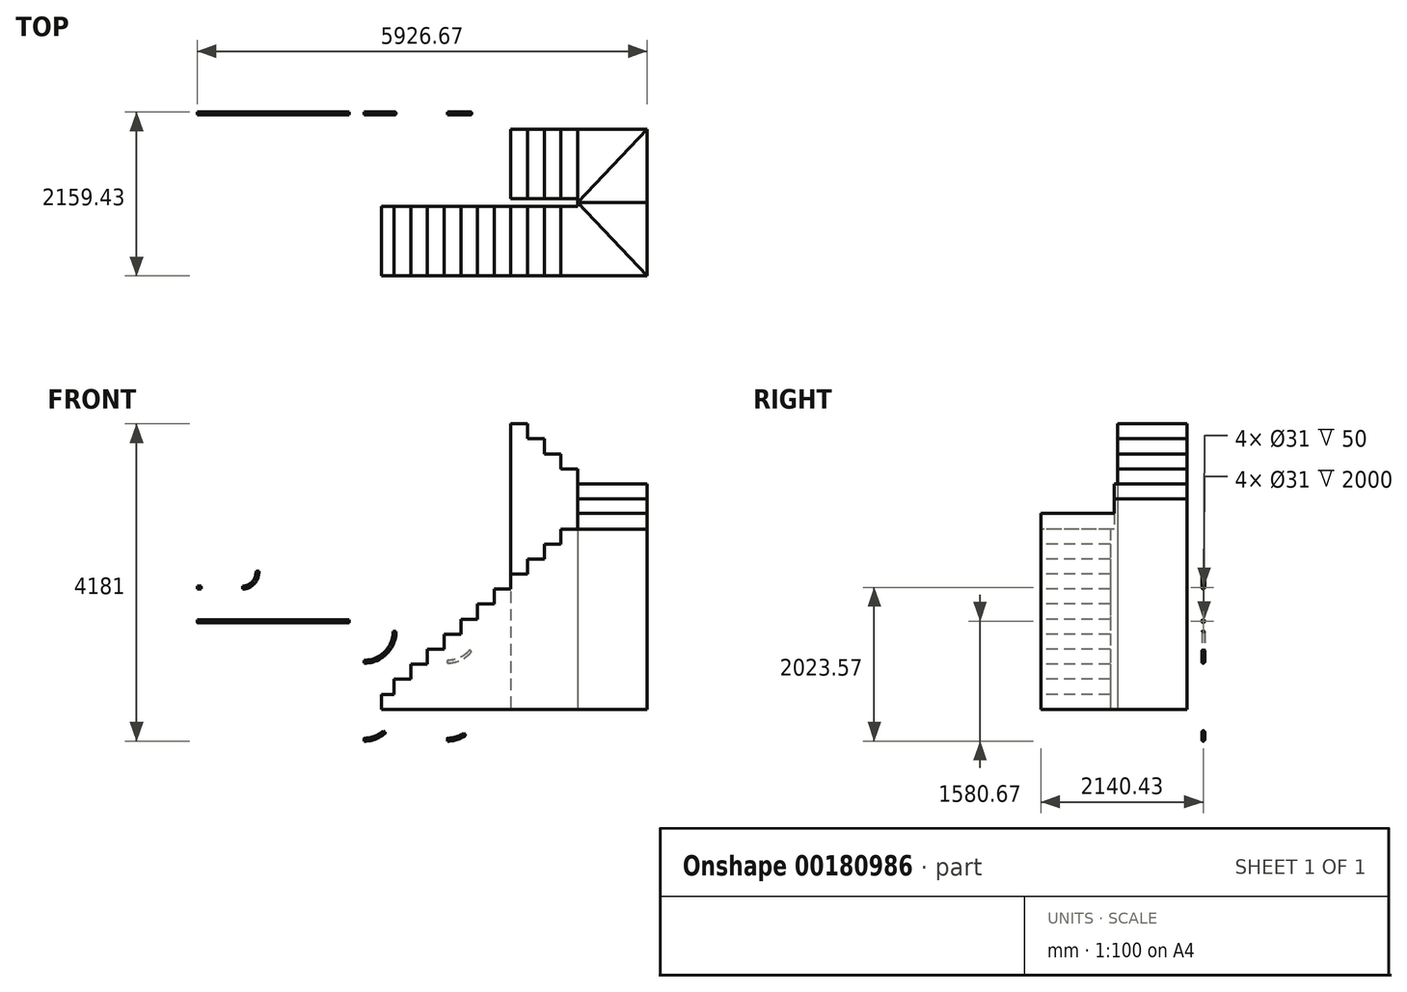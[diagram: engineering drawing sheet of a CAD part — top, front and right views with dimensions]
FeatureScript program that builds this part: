
annotation { "Feature Type Name" : "Feature", "Feature Type Description" : "" }
export const myFeature = defineFeature(function(context is Context, id is Id, definition is map)
    precondition{}
    {
        {
            var Q0;
            Q0=qCreatedBy(makeId("Front.planeOp"),FACE);
            var sketch = newSketch(context, id + "F0", { "sketchPlane" : qUnion([Q0])});
            skArc(sketch, "E0", {"start": v(-72.1, -400) * mm, "mid": v(71.25, -373.43) * mm, "end": v(195.56, -297.26) * mm});
            skArc(sketch, "E1", {"start": v(1022.64, -400) * mm, "mid": v(1142.93, -381.49) * mm, "end": v(1252.07, -327.66) * mm});
            skArc(sketch, "E2", {"start": v(-72.1, 626.56) * mm, "mid": v(210.75, 743.72) * mm, "end": v(327.9, 1026.56) * mm});
            skArc(sketch, "E3", {"start": v(1022.64, 626.56) * mm, "mid": v(1191.7, 664.04) * mm, "end": v(1329.06, 769.45) * mm});
            skLineSegment(sketch, "E4", {"start": v(-72.1, 645.56) * mm, "end": v(-72.1, 607.56) * mm});
            skLineSegment(sketch, "E5", {"start": v(308.9, 1026.56) * mm, "end": v(346.9, 1026.56) * mm});
            skLineSegment(sketch, "E6", {"start": v(-72.1, -381) * mm, "end": v(-72.1, -419) * mm});
            skLineSegment(sketch, "E7", {"start": v(182.84, -283.14) * mm, "end": v(208.27, -311.38) * mm});
            skLineSegment(sketch, "E8", {"start": v(1022.64, 645.56) * mm, "end": v(1022.64, 607.56) * mm});
            skLineSegment(sketch, "E9", {"start": v(1314.5, 781.66) * mm, "end": v(1343.62, 757.24) * mm});
            skLineSegment(sketch, "E10", {"start": v(1022.64, -381) * mm, "end": v(1022.64, -419) * mm});
            skLineSegment(sketch, "E11", {"start": v(1241.18, -312.1) * mm, "end": v(1262.97, -343.22) * mm});
            skArc(sketch, "E12.0", {"start": v(-72.1, 607.56) * mm, "mid": v(224.18, 730.29) * mm, "end": v(346.9, 1026.56) * mm});
            skArc(sketch, "E13.0", {"start": v(-72.1, 645.56) * mm, "mid": v(197.31, 757.16) * mm, "end": v(308.9, 1026.56) * mm});
            skArc(sketch, "E14.0", {"start": v(1022.64, 607.56) * mm, "mid": v(1199.72, 646.82) * mm, "end": v(1343.62, 757.24) * mm});
            skArc(sketch, "E15.0", {"start": v(1022.64, 645.56) * mm, "mid": v(1183.66, 681.26) * mm, "end": v(1314.5, 781.66) * mm});
            skArc(sketch, "E16.0", {"start": v(1022.64, -419) * mm, "mid": v(1148.64, -399.6) * mm, "end": v(1262.97, -343.22) * mm});
            skArc(sketch, "E17.0", {"start": v(1022.64, -381) * mm, "mid": v(1137.21, -363.37) * mm, "end": v(1241.18, -312.1) * mm});
            skArc(sketch, "E18.0", {"start": v(-72.1, -419) * mm, "mid": v(78.06, -391.17) * mm, "end": v(208.27, -311.38) * mm});
            skArc(sketch, "E19.0", {"start": v(-72.1, -381) * mm, "mid": v(64.44, -355.7) * mm, "end": v(182.84, -283.14) * mm});
            skSolve(sketch);
        }
        {
            var Q0;
            Q0=sQuery(id+"F0.wireOp",VERTEX,"E2.start");
            var Q1;
            Q1=qCreatedBy(makeId("Right.planeOp"),FACE);
            cPlane(context, id + "F1", {"entities" : qUnion([Q0, Q1]), "cplaneType" : CPlaneType.PLANE_POINT, "offset" : 25 * mm, "width" : 150 * mm, "height" : 150 * mm});
        }
        {
            var Q0;
            Q0=qCreatedBy(id+"F1.planeOp",FACE);
            var sketch = newSketch(context, id + "F2", { "sketchPlane" : qUnion([Q0])});
            skCircle(sketch, "E20", {"center": v(0, 626.56) * mm, "radius": 19 * mm});
            skCircle(sketch, "E21.0", {"center": v(0, 626.56) * mm, "radius": 15.5 * mm});
            skSolve(sketch);
        }
        {
            var Q0;
            Q0=qCreatedBy(makeId("Right.planeOp"),FACE);
            var Q1;
            Q1=sQuery(id+"F0.wireOp",VERTEX,"E0.start");
            cPlane(context, id + "F3", {"entities" : qUnion([Q0, Q1]), "cplaneType" : CPlaneType.PLANE_POINT, "offset" : 25 * mm, "width" : 150 * mm, "height" : 150 * mm});
        }
        {
            var Q0;
            Q0=qCreatedBy(id+"F3.planeOp",FACE);
            var sketch = newSketch(context, id + "F4", { "sketchPlane" : qUnion([Q0])});
            skCircle(sketch, "E22", {"center": v(0, -400) * mm, "radius": 19 * mm});
            skCircle(sketch, "E23.0", {"center": v(0, -400) * mm, "radius": 15.2 * mm});
            skSolve(sketch);
        }
        {
            var Q0;
            Q0=qCreatedBy(makeId("Right.planeOp"),FACE);
            var Q1;
            Q1=sQuery(id+"F0.wireOp",VERTEX,"E3.start");
            cPlane(context, id + "F5", {"entities" : qUnion([Q0, Q1]), "cplaneType" : CPlaneType.PLANE_POINT, "offset" : 25 * mm, "width" : 150 * mm, "height" : 150 * mm});
        }
        {
            var Q0;
            Q0=qCreatedBy(id+"F5.planeOp",FACE);
            var sketch = newSketch(context, id + "F6", { "sketchPlane" : qUnion([Q0])});
            skCircle(sketch, "E24", {"center": v(0, 626.56) * mm, "radius": 19 * mm});
            skCircle(sketch, "E25.0", {"center": v(0, 626.56) * mm, "radius": 15.5 * mm});
            skSolve(sketch);
        }
        {
            var Q0;
            Q0=sQuery(id+"F0.wireOp",VERTEX,"E1.start");
            var Q1;
            Q1=qCreatedBy(makeId("Right.planeOp"),FACE);
            cPlane(context, id + "F7", {"entities" : qUnion([Q0, Q1]), "cplaneType" : CPlaneType.PLANE_POINT, "offset" : 25 * mm, "width" : 150 * mm, "height" : 150 * mm});
        }
        {
            var Q0;
            Q0=qCreatedBy(id+"F7.planeOp",FACE);
            var sketch = newSketch(context, id + "F8", { "sketchPlane" : qUnion([Q0])});
            skCircle(sketch, "E26", {"center": v(0, -400) * mm, "radius": 19 * mm});
            skCircle(sketch, "E27.0", {"center": v(0, -400) * mm, "radius": 15.5 * mm});
            skSolve(sketch);
        }
        {
            var Q0;
            Q0=makeQuery(id+"F8.imprint","IMPRINT",FACE,{"disambiguationData":[TD([[makeQuery(id+"F8.imprint","IMPRINT",EDGE,{"derivedFrom":sQuery(id+"F8.wireOp",EDGE,"E26")}),1.0]])]});
            var Q1;
            Q1=sQuery(id+"F0.wireOp",EDGE,"E1");
            sweep(context, id + "F9", {"profiles" : qUnion([Q0]), "path" : qUnion([Q1])});
        }
        {
            var Q0;
            Q0=makeQuery(id+"F6.imprint","IMPRINT",FACE,{"disambiguationData":[TD([[makeQuery(id+"F6.imprint","IMPRINT",EDGE,{"derivedFrom":sQuery(id+"F6.wireOp",EDGE,"E24")}),1.0]])]});
            var Q1;
            Q1=sQuery(id+"F0.wireOp",EDGE,"E3");
            sweep(context, id + "F10", {"profiles" : qUnion([Q0]), "path" : qUnion([Q1])});
        }
        {
            var Q0;
            Q0=makeQuery(id+"F2.imprint","IMPRINT",FACE,{"disambiguationData":[TD([[makeQuery(id+"F2.imprint","IMPRINT",EDGE,{"derivedFrom":sQuery(id+"F2.wireOp",EDGE,"E20")}),1.0]])]});
            var Q1;
            Q1=sQuery(id+"F0.wireOp",EDGE,"E2");
            sweep(context, id + "F11", {"profiles" : qUnion([Q0]), "path" : qUnion([Q1])});
        }
        {
            var Q0;
            Q0=makeQuery(id+"F4.imprint","IMPRINT",FACE,{"disambiguationData":[TD([[makeQuery(id+"F4.imprint","IMPRINT",EDGE,{"derivedFrom":sQuery(id+"F4.wireOp",EDGE,"E22")}),1.0]])]});
            var Q1;
            Q1=sQuery(id+"F0.wireOp",EDGE,"E0");
            sweep(context, id + "F12", {"profiles" : qUnion([Q0]), "path" : qUnion([Q1])});
        }
        {
            var Q0;
            Q0=qCreatedBy(makeId("Top.planeOp"),FACE);
            var sketch = newSketch(context, id + "F13", { "sketchPlane" : qUnion([Q0])});
            skLineSegment(sketch, "E28.bottom", {"start": v(155.18, -210.43) * mm, "end": v(3655.18, -210.43) * mm});
            skLineSegment(sketch, "E28.top", {"start": v(155.18, -2140.43) * mm, "end": v(3655.18, -2140.43) * mm});
            skLineSegment(sketch, "E28.left", {"start": v(155.18, -210.43) * mm, "end": v(155.18, -2140.43) * mm});
            skLineSegment(sketch, "E28.right", {"start": v(3655.18, -210.43) * mm, "end": v(3655.18, -2140.43) * mm});
            skLineSegment(sketch, "E29", {"start": v(155.18, -1175.43) * mm, "end": v(2740.18, -1175.43) * mm, "construction": true});
            skLineSegment(sketch, "E30", {"start": v(155.18, -1125.43) * mm, "end": v(2740.18, -1125.43) * mm});
            skLineSegment(sketch, "E31", {"start": v(2740.18, -1125.43) * mm, "end": v(2740.18, -1175.43) * mm});
            skLineSegment(sketch, "E32", {"start": v(155.18, -1225.43) * mm, "end": v(2740.18, -1225.43) * mm});
            skLineSegment(sketch, "E33", {"start": v(2740.18, -1225.43) * mm, "end": v(2740.18, -1175.43) * mm});
            skLineSegment(sketch, "E34", {"start": v(2740.18, -1125.43) * mm, "end": v(2740.18, -210.43) * mm});
            skLineSegment(sketch, "E35", {"start": v(2740.18, -1225.43) * mm, "end": v(2740.18, -2140.43) * mm});
            skLineSegment(sketch, "E36", {"start": v(2740.18, -1175.43) * mm, "end": v(3655.18, -210.43) * mm});
            skLineSegment(sketch, "E37", {"start": v(2740.18, -1175.43) * mm, "end": v(3655.18, -2140.43) * mm});
            skPoint(sketch, "E38.orphan", {"position": v(3655.18, -1175.43) * mm});
            skLineSegment(sketch, "E39", {"start": v(2740.18, -1175.43) * mm, "end": v(3655.18, -1175.43) * mm});
            skLineSegment(sketch, "E40", {"start": v(2520.18, -210.43) * mm, "end": v(2520.18, -2140.43) * mm});
            skLineSegment(sketch, "E41", {"start": v(2300.18, -210.43) * mm, "end": v(2300.18, -2140.43) * mm});
            skLineSegment(sketch, "E42", {"start": v(2080.18, -210.43) * mm, "end": v(2080.18, -2140.43) * mm});
            skLineSegment(sketch, "E43", {"start": v(1860.18, -210.43) * mm, "end": v(1860.18, -2140.43) * mm});
            skLineSegment(sketch, "E44", {"start": v(1640.18, -210.43) * mm, "end": v(1640.18, -2140.43) * mm});
            skLineSegment(sketch, "E45", {"start": v(1420.18, -210.43) * mm, "end": v(1420.18, -2140.43) * mm});
            skLineSegment(sketch, "E46", {"start": v(1200.18, -210.43) * mm, "end": v(1200.18, -2140.43) * mm});
            skLineSegment(sketch, "E47", {"start": v(980.18, -210.43) * mm, "end": v(980.18, -2140.43) * mm});
            skLineSegment(sketch, "E48", {"start": v(760.18, -210.43) * mm, "end": v(760.18, -2140.43) * mm});
            skLineSegment(sketch, "E49", {"start": v(540.18, -210.43) * mm, "end": v(540.18, -2140.43) * mm});
            skLineSegment(sketch, "E50", {"start": v(320.18, -210.43) * mm, "end": v(320.18, -2140.43) * mm});
            skSolve(sketch);
        }
        {
            var Q0;
            {var subQ0=sQuery(id+"F13.wireOp",EDGE,"E28.left");var subQ1=sQuery(id+"F13.wireOp",EDGE,"E28.top");var subQ2=makeQuery(id+"F13.imprint","INTERSECT",VERTEX,{"derivedFrom":[subQ1,subQ0]});Q0=makeQuery(id+"F13.imprint","IMPRINT",FACE,{"disambiguationData":[TD([[makeQuery(id+"F13.imprint","IMPRINT",EDGE,{"disambiguationData":[TD([[subQ2,-1.0]])],"derivedFrom":subQ1}),1.0]])]});}
            extrude(context, id + "F14", {"entities" : qUnion([Q0]), "depth" : 198 * mm});
        }
        {
            var Q0;
            {var subQ0=sQuery(id+"F13.wireOp",EDGE,"E49");var subQ1=sQuery(id+"F13.wireOp",EDGE,"E28.top");var subQ2=makeQuery(id+"F13.imprint","INTERSECT",VERTEX,{"derivedFrom":[subQ1,subQ0]});Q0=makeQuery(id+"F13.imprint","IMPRINT",FACE,{"disambiguationData":[TD([[makeQuery(id+"F13.imprint","IMPRINT",EDGE,{"disambiguationData":[TD([[subQ2,1.0]])],"derivedFrom":subQ1}),1.0]])]});}
            extrude(context, id + "F15", {"entities" : qUnion([Q0]), "operationType" : NewBodyOperationType.ADD, "depth" : (198 * 2) * mm});
        }
        {
            var Q0;
            {var subQ0=sQuery(id+"F13.wireOp",EDGE,"E48");var subQ1=sQuery(id+"F13.wireOp",EDGE,"E28.top");var subQ2=makeQuery(id+"F13.imprint","INTERSECT",VERTEX,{"derivedFrom":[subQ1,subQ0]});Q0=makeQuery(id+"F13.imprint","IMPRINT",FACE,{"disambiguationData":[TD([[makeQuery(id+"F13.imprint","IMPRINT",EDGE,{"disambiguationData":[TD([[subQ2,1.0]])],"derivedFrom":subQ1}),1.0]])]});}
            extrude(context, id + "F16", {"entities" : qUnion([Q0]), "operationType" : NewBodyOperationType.ADD, "depth" : (198 * 3) * mm});
        }
        {
            var Q0;
            {var subQ0=sQuery(id+"F13.wireOp",EDGE,"E47");var subQ1=sQuery(id+"F13.wireOp",EDGE,"E28.top");var subQ2=makeQuery(id+"F13.imprint","INTERSECT",VERTEX,{"derivedFrom":[subQ1,subQ0]});Q0=makeQuery(id+"F13.imprint","IMPRINT",FACE,{"disambiguationData":[TD([[makeQuery(id+"F13.imprint","IMPRINT",EDGE,{"disambiguationData":[TD([[subQ2,1.0]])],"derivedFrom":subQ1}),1.0]])]});}
            extrude(context, id + "F17", {"entities" : qUnion([Q0]), "operationType" : NewBodyOperationType.ADD, "depth" : (198 * 4) * mm});
        }
        {
            var Q0;
            {var subQ0=sQuery(id+"F13.wireOp",EDGE,"E46");var subQ1=sQuery(id+"F13.wireOp",EDGE,"E28.top");var subQ2=makeQuery(id+"F13.imprint","INTERSECT",VERTEX,{"derivedFrom":[subQ1,subQ0]});Q0=makeQuery(id+"F13.imprint","IMPRINT",FACE,{"disambiguationData":[TD([[makeQuery(id+"F13.imprint","IMPRINT",EDGE,{"disambiguationData":[TD([[subQ2,1.0]])],"derivedFrom":subQ1}),1.0]])]});}
            extrude(context, id + "F18", {"entities" : qUnion([Q0]), "operationType" : NewBodyOperationType.ADD, "depth" : (198 * 5) * mm});
        }
        {
            var Q0;
            {var subQ0=sQuery(id+"F13.wireOp",EDGE,"E45");var subQ1=sQuery(id+"F13.wireOp",EDGE,"E28.top");var subQ2=makeQuery(id+"F13.imprint","INTERSECT",VERTEX,{"derivedFrom":[subQ1,subQ0]});Q0=makeQuery(id+"F13.imprint","IMPRINT",FACE,{"disambiguationData":[TD([[makeQuery(id+"F13.imprint","IMPRINT",EDGE,{"disambiguationData":[TD([[subQ2,1.0]])],"derivedFrom":subQ1}),1.0]])]});}
            extrude(context, id + "F19", {"entities" : qUnion([Q0]), "operationType" : NewBodyOperationType.ADD, "depth" : (198 * 6) * mm});
        }
        {
            var Q0;
            {var subQ0=sQuery(id+"F13.wireOp",EDGE,"E44");var subQ1=sQuery(id+"F13.wireOp",EDGE,"E28.top");var subQ2=makeQuery(id+"F13.imprint","INTERSECT",VERTEX,{"derivedFrom":[subQ1,subQ0]});Q0=makeQuery(id+"F13.imprint","IMPRINT",FACE,{"disambiguationData":[TD([[makeQuery(id+"F13.imprint","IMPRINT",EDGE,{"disambiguationData":[TD([[subQ2,1.0]])],"derivedFrom":subQ1}),1.0]])]});}
            extrude(context, id + "F20", {"entities" : qUnion([Q0]), "operationType" : NewBodyOperationType.ADD, "depth" : (198 * 7) * mm});
        }
        {
            var Q0;
            {var subQ0=sQuery(id+"F13.wireOp",EDGE,"E43");var subQ1=sQuery(id+"F13.wireOp",EDGE,"E28.top");var subQ2=makeQuery(id+"F13.imprint","INTERSECT",VERTEX,{"derivedFrom":[subQ1,subQ0]});Q0=makeQuery(id+"F13.imprint","IMPRINT",FACE,{"disambiguationData":[TD([[makeQuery(id+"F13.imprint","IMPRINT",EDGE,{"disambiguationData":[TD([[subQ2,1.0]])],"derivedFrom":subQ1}),1.0]])]});}
            extrude(context, id + "F21", {"entities" : qUnion([Q0]), "operationType" : NewBodyOperationType.ADD, "depth" : (198 * 8) * mm});
        }
        {
            var Q0;
            {var subQ0=sQuery(id+"F13.wireOp",EDGE,"E42");var subQ1=sQuery(id+"F13.wireOp",EDGE,"E28.top");var subQ2=makeQuery(id+"F13.imprint","INTERSECT",VERTEX,{"derivedFrom":[subQ1,subQ0]});Q0=makeQuery(id+"F13.imprint","IMPRINT",FACE,{"disambiguationData":[TD([[makeQuery(id+"F13.imprint","IMPRINT",EDGE,{"disambiguationData":[TD([[subQ2,1.0]])],"derivedFrom":subQ1}),1.0]])]});}
            extrude(context, id + "F22", {"entities" : qUnion([Q0]), "operationType" : NewBodyOperationType.ADD, "depth" : (198 * 9) * mm});
        }
        {
            var Q0;
            {var subQ0=sQuery(id+"F13.wireOp",EDGE,"E41");var subQ1=sQuery(id+"F13.wireOp",EDGE,"E28.top");var subQ2=makeQuery(id+"F13.imprint","INTERSECT",VERTEX,{"derivedFrom":[subQ1,subQ0]});Q0=makeQuery(id+"F13.imprint","IMPRINT",FACE,{"disambiguationData":[TD([[makeQuery(id+"F13.imprint","IMPRINT",EDGE,{"disambiguationData":[TD([[subQ2,1.0]])],"derivedFrom":subQ1}),1.0]])]});}
            extrude(context, id + "F23", {"entities" : qUnion([Q0]), "operationType" : NewBodyOperationType.ADD, "depth" : (198 * 10) * mm});
        }
        {
            var Q0;
            {var subQ0=sQuery(id+"F13.wireOp",EDGE,"E40");var subQ1=sQuery(id+"F13.wireOp",EDGE,"E28.top");var subQ2=makeQuery(id+"F13.imprint","INTERSECT",VERTEX,{"derivedFrom":[subQ1,subQ0]});Q0=makeQuery(id+"F13.imprint","IMPRINT",FACE,{"disambiguationData":[TD([[makeQuery(id+"F13.imprint","IMPRINT",EDGE,{"disambiguationData":[TD([[subQ2,1.0]])],"derivedFrom":subQ1}),1.0]])]});}
            extrude(context, id + "F24", {"entities" : qUnion([Q0]), "operationType" : NewBodyOperationType.ADD, "depth" : (198 * 11) * mm});
        }
        {
            var Q0;
            {var subQ0=sQuery(id+"F13.wireOp",EDGE,"E35");Q0=makeQuery(id+"F13.imprint","IMPRINT",FACE,{"disambiguationData":[TD([[makeQuery(id+"F13.imprint","IMPRINT",EDGE,{"derivedFrom":subQ0}),-1.0]])]});}
            extrude(context, id + "F25", {"entities" : qUnion([Q0]), "operationType" : NewBodyOperationType.ADD, "depth" : (198 * 12) * mm});
        }
        {
            var Q0;
            Q0=makeQuery(id+"F13.imprint","IMPRINT",FACE,{"disambiguationData":[TD([[makeQuery(id+"F13.imprint","IMPRINT",EDGE,{"derivedFrom":sQuery(id+"F13.wireOp",EDGE,"E33")}),-1.0]])]});
            extrude(context, id + "F26", {"entities" : qUnion([Q0]), "operationType" : NewBodyOperationType.ADD, "depth" : (198 * 12) * mm});
        }
        {
            var Q0;
            {var subQ0=sQuery(id+"F13.wireOp",EDGE,"E37");Q0=makeQuery(id+"F13.imprint","IMPRINT",FACE,{"disambiguationData":[TD([[makeQuery(id+"F13.imprint","IMPRINT",EDGE,{"derivedFrom":subQ0}),1.0]])]});}
            extrude(context, id + "F27", {"entities" : qUnion([Q0]), "operationType" : NewBodyOperationType.ADD, "depth" : 2584 * mm});
        }
        {
            var Q0;
            {var subQ0=sQuery(id+"F13.wireOp",EDGE,"E36");Q0=makeQuery(id+"F13.imprint","IMPRINT",FACE,{"disambiguationData":[TD([[makeQuery(id+"F13.imprint","IMPRINT",EDGE,{"derivedFrom":subQ0}),-1.0]])]});}
            extrude(context, id + "F28", {"entities" : qUnion([Q0]), "operationType" : NewBodyOperationType.ADD, "depth" : (198 * 14) * mm});
        }
        {
            var Q0;
            Q0=makeQuery(id+"F13.imprint","IMPRINT",FACE,{"disambiguationData":[TD([[makeQuery(id+"F13.imprint","IMPRINT",EDGE,{"derivedFrom":sQuery(id+"F13.wireOp",EDGE,"E31")}),1.0]])]});
            extrude(context, id + "F29", {"entities" : qUnion([Q0]), "operationType" : NewBodyOperationType.ADD, "depth" : (198 * 15) * mm});
        }
        {
            var Q0;
            {var subQ0=sQuery(id+"F13.wireOp",EDGE,"E34");Q0=makeQuery(id+"F13.imprint","IMPRINT",FACE,{"disambiguationData":[TD([[makeQuery(id+"F13.imprint","IMPRINT",EDGE,{"derivedFrom":subQ0}),1.0]])]});}
            extrude(context, id + "F30", {"entities" : qUnion([Q0]), "operationType" : NewBodyOperationType.ADD, "depth" : (198 * 16) * mm});
        }
        {
            var Q0;
            {var subQ0=sQuery(id+"F13.wireOp",EDGE,"E40");var subQ1=sQuery(id+"F13.wireOp",EDGE,"E28.bottom");var subQ2=makeQuery(id+"F13.imprint","INTERSECT",VERTEX,{"derivedFrom":[subQ1,subQ0]});Q0=makeQuery(id+"F13.imprint","IMPRINT",FACE,{"disambiguationData":[TD([[makeQuery(id+"F13.imprint","IMPRINT",EDGE,{"disambiguationData":[TD([[subQ2,1.0]])],"derivedFrom":subQ1}),-1.0]])]});}
            extrude(context, id + "F31", {"entities" : qUnion([Q0]), "operationType" : NewBodyOperationType.ADD, "depth" : (198 * 17) * mm});
        }
        {
            var Q0;
            {var subQ0=sQuery(id+"F13.wireOp",EDGE,"E41");var subQ1=sQuery(id+"F13.wireOp",EDGE,"E28.bottom");var subQ2=makeQuery(id+"F13.imprint","INTERSECT",VERTEX,{"derivedFrom":[subQ1,subQ0]});Q0=makeQuery(id+"F13.imprint","IMPRINT",FACE,{"disambiguationData":[TD([[makeQuery(id+"F13.imprint","IMPRINT",EDGE,{"disambiguationData":[TD([[subQ2,1.0]])],"derivedFrom":subQ1}),-1.0]])]});}
            extrude(context, id + "F32", {"entities" : qUnion([Q0]), "operationType" : NewBodyOperationType.ADD, "depth" : (198 * 18) * mm});
        }
        {
            var Q0;
            {var subQ0=sQuery(id+"F13.wireOp",EDGE,"E42");var subQ1=sQuery(id+"F13.wireOp",EDGE,"E28.bottom");var subQ2=makeQuery(id+"F13.imprint","INTERSECT",VERTEX,{"derivedFrom":[subQ1,subQ0]});Q0=makeQuery(id+"F13.imprint","IMPRINT",FACE,{"disambiguationData":[TD([[makeQuery(id+"F13.imprint","IMPRINT",EDGE,{"disambiguationData":[TD([[subQ2,1.0]])],"derivedFrom":subQ1}),-1.0]])]});}
            extrude(context, id + "F33", {"entities" : qUnion([Q0]), "operationType" : NewBodyOperationType.ADD, "depth" : (198 * 19) * mm});
        }
        {
            var Q0;
            Q0=qCreatedBy(makeId("Front.planeOp"),FACE);
            var sketch = newSketch(context, id + "F34", { "sketchPlane" : qUnion([Q0])});
            skLineSegment(sketch, "E51", {"start": v(-2271.49, 1604.57) * mm, "end": v(-2221.49, 1604.57) * mm});
            skArc(sketch, "E52", {"start": v(-1672.01, 1604.57) * mm, "mid": v(-1529.27, 1671.95) * mm, "end": v(-1479.85, 1821.87) * mm});
            skLineSegment(sketch, "E53", {"start": v(-2271.49, 1161.67) * mm, "end": v(-271.49, 1161.67) * mm});
            skSolve(sketch);
        }
        {
            var Q0;
            Q0=qCreatedBy(makeId("Right.planeOp"),FACE);
            var Q1;
            Q1=sQuery(id+"F34.wireOp",VERTEX,"E51.start");
            cPlane(context, id + "F35", {"entities" : qUnion([Q0, Q1]), "cplaneType" : CPlaneType.PLANE_POINT, "offset" : 25 * mm, "width" : 150 * mm, "height" : 150 * mm});
        }
        {
            var Q0;
            Q0=qCreatedBy(id+"F35.planeOp",FACE);
            var sketch = newSketch(context, id + "F36", { "sketchPlane" : qUnion([Q0])});
            skCircle(sketch, "E54", {"center": v(0, 1604.57) * mm, "radius": 19 * mm});
            skCircle(sketch, "E55.0", {"center": v(0, 1604.57) * mm, "radius": 15.5 * mm});
            skSolve(sketch);
        }
        {
            var Q0;
            Q0=sQuery(id+"F34.wireOp",VERTEX,"E52.start");
            var Q1;
            Q1=qCreatedBy(makeId("Right.planeOp"),FACE);
            cPlane(context, id + "F37", {"entities" : qUnion([Q0, Q1]), "cplaneType" : CPlaneType.PLANE_POINT, "offset" : 25 * mm, "width" : 150 * mm, "height" : 150 * mm});
        }
        {
            var Q0;
            Q0=qCreatedBy(id+"F37.planeOp",FACE);
            var sketch = newSketch(context, id + "F38", { "sketchPlane" : qUnion([Q0])});
            skCircle(sketch, "E56", {"center": v(0, 1604.57) * mm, "radius": 19 * mm});
            skCircle(sketch, "E57.0", {"center": v(0, 1604.57) * mm, "radius": 15.5 * mm});
            skSolve(sketch);
        }
        {
            var Q0;
            Q0=qCreatedBy(makeId("Right.planeOp"),FACE);
            var Q1;
            Q1=sQuery(id+"F34.wireOp",VERTEX,"E53.start");
            cPlane(context, id + "F39", {"entities" : qUnion([Q0, Q1]), "cplaneType" : CPlaneType.PLANE_POINT, "offset" : 25 * mm, "width" : 150 * mm, "height" : 150 * mm});
        }
        {
            var Q0;
            Q0=qCreatedBy(id+"F39.planeOp",FACE);
            var sketch = newSketch(context, id + "F40", { "sketchPlane" : qUnion([Q0])});
            skCircle(sketch, "E58", {"center": v(0, 1161.67) * mm, "radius": 19 * mm});
            skCircle(sketch, "E59.0", {"center": v(0, 1161.67) * mm, "radius": 15.5 * mm});
            skSolve(sketch);
        }
        {
            var Q0;
            Q0=makeQuery(id+"F36.imprint","IMPRINT",FACE,{"disambiguationData":[TD([[makeQuery(id+"F36.imprint","IMPRINT",EDGE,{"derivedFrom":sQuery(id+"F36.wireOp",EDGE,"E54")}),1.0]])]});
            var Q1;
            Q1=sQuery(id+"F34.wireOp",EDGE,"E51");
            sweep(context, id + "F41", {"profiles" : qUnion([Q0]), "path" : qUnion([Q1])});
        }
        {
            var Q0;
            Q0=makeQuery(id+"F38.imprint","IMPRINT",FACE,{"disambiguationData":[TD([[makeQuery(id+"F38.imprint","IMPRINT",EDGE,{"derivedFrom":sQuery(id+"F38.wireOp",EDGE,"E56")}),1.0]])]});
            var Q1;
            Q1=sQuery(id+"F34.wireOp",EDGE,"E52");
            sweep(context, id + "F42", {"profiles" : qUnion([Q0]), "path" : qUnion([Q1])});
        }
        {
            var Q0;
            Q0=makeQuery(id+"F40.imprint","IMPRINT",FACE,{"disambiguationData":[TD([[makeQuery(id+"F40.imprint","IMPRINT",EDGE,{"derivedFrom":sQuery(id+"F40.wireOp",EDGE,"E58")}),1.0]])]});
            var Q1;
            Q1=sQuery(id+"F34.wireOp",EDGE,"E53");
            sweep(context, id + "F43", {"profiles" : qUnion([Q0]), "path" : qUnion([Q1])});
        }
    });
